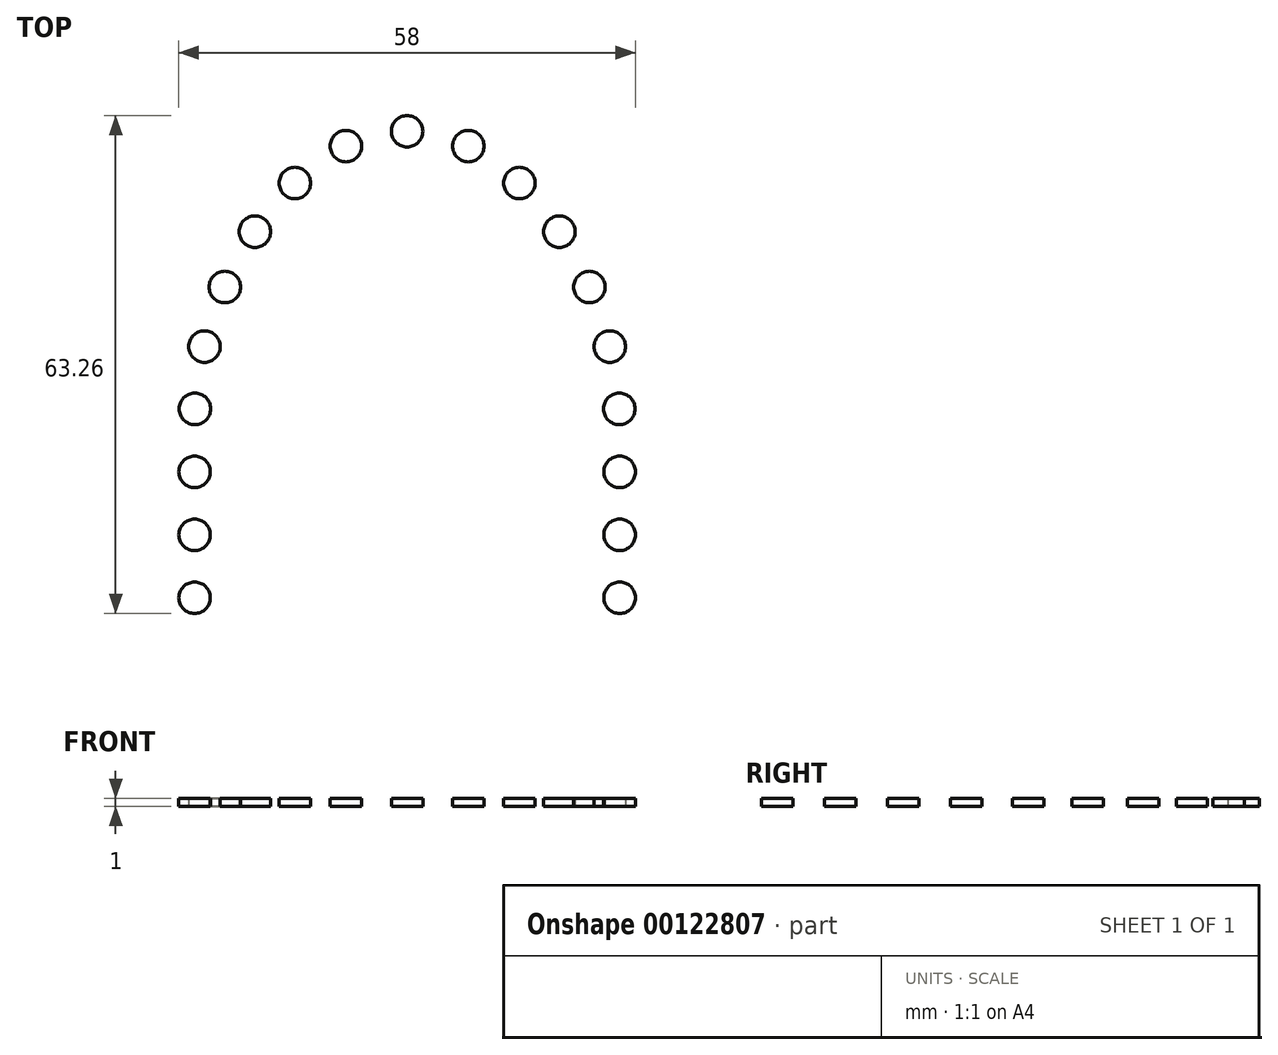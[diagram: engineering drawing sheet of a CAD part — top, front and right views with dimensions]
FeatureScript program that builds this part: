
annotation { "Feature Type Name" : "Feature", "Feature Type Description" : "" }
export const myFeature = defineFeature(function(context is Context, id is Id, definition is map)
    precondition{}
    {
        {
            var Q0;
            Q0=qCreatedBy(makeId("Top.planeOp"),FACE);
            var sketch = newSketch(context, id + "F0", { "sketchPlane" : qUnion([Q0])});
            skLineSegment(sketch, "E0.top", {"start": v(-35, -35) * mm, "end": v(35, -35) * mm});
            skPoint(sketch, "E0.middle", {"position": v(0, 13.14) * mm});
            skPoint(sketch, "E1", {"position": v(0, 0) * mm});
            skCircle(sketch, "E2", {"center": v(0, 0) * mm, "radius": 35 * mm});
            skPoint(sketch, "E3.visualSharp", {"position": v(-35, -35) * mm});
            skPoint(sketch, "E4.visualSharp", {"position": v(35, -35) * mm});
            skPoint(sketch, "E5", {"position": v(-35, 0) * mm});
            skPoint(sketch, "E6", {"position": v(35, 0) * mm});
            skFitSpline(sketch, "E7", {"points": [v(0, 45) * mm, v(-35, 0) * mm], "startDerivative": vector(-60.6, 0) * mm, "endDerivative": vector(0, -60.15) * mm});
            skLineSegment(sketch, "E8", {"start": v(-35, 0) * mm, "end": v(-35, -35) * mm});
            skLineSegment(sketch, "E9", {"start": v(35, 0) * mm, "end": v(35, -35) * mm});
            skFitSpline(sketch, "E10.MirrorCS", {"points": [v(0, 45) * mm, v(35, 0) * mm], "startDerivative": vector(60.6, 0) * mm, "endDerivative": vector(0, -60.15) * mm});
            skFitSpline(sketch, "E11.0", {"points": [v(0, 37) * mm, v(-0.85, 37) * mm, v(-2.51, 36.87) * mm, v(-4.95, 36.3) * mm, v(-7.36, 35.37) * mm, v(-10.54, 33.64) * mm, v(-14.42, 30.55) * mm, v(-18.67, 25.54) * mm, v(-22.24, 19.56) * mm, v(-24.95, 13) * mm, v(-26.62, 6.3) * mm, v(-27, 2.01) * mm, v(-27, 0) * mm]});
            skPoint(sketch, "E12", {"position": v(0, 37) * mm});
            skPoint(sketch, "E13", {"position": v(-7.77, 35.11) * mm});
            skPoint(sketch, "E14", {"position": v(-14.26, 30.43) * mm});
            skPoint(sketch, "E15", {"position": v(-19.34, 24.24) * mm});
            skPoint(sketch, "E16", {"position": v(-23.15, 17.21) * mm});
            skPoint(sketch, "E17", {"position": v(-25.74, 9.64) * mm});
            skLineSegment(sketch, "E18", {"start": v(-27, 0) * mm, "end": v(-27, -35) * mm});
            skPoint(sketch, "E19", {"position": v(-26.96, 1.74) * mm});
            skPoint(sketch, "E20", {"position": v(-27, -6.26) * mm});
            skPoint(sketch, "E21", {"position": v(-27, -14.26) * mm});
            skPoint(sketch, "E22", {"position": v(-27, -22.26) * mm});
            skPoint(sketch, "E23", {"position": v(-27, -30.26) * mm});
            skLineSegment(sketch, "E24.MirrorCS", {"start": v(27, 0) * mm, "end": v(27, -35) * mm});
            skPoint(sketch, "E25.MirrorP", {"position": v(7.77, 35.11) * mm});
            skPoint(sketch, "E26.MirrorP", {"position": v(14.26, 30.43) * mm});
            skPoint(sketch, "E27.MirrorP", {"position": v(19.34, 24.24) * mm});
            skPoint(sketch, "E28.MirrorP", {"position": v(23.15, 17.21) * mm});
            skPoint(sketch, "E29.MirrorP", {"position": v(25.74, 9.64) * mm});
            skPoint(sketch, "E30.MirrorP", {"position": v(26.96, 1.74) * mm});
            skPoint(sketch, "E31.MirrorP", {"position": v(27, -6.26) * mm});
            skPoint(sketch, "E32.MirrorP", {"position": v(27, -14.26) * mm});
            skPoint(sketch, "E33.MirrorP", {"position": v(27, -22.26) * mm});
            skPoint(sketch, "E34.MirrorP", {"position": v(27, -30.26) * mm});
            skFitSpline(sketch, "E35.0", {"points": [v(0, 37) * mm, v(0.85, 37) * mm, v(2.51, 36.87) * mm, v(4.95, 36.3) * mm, v(7.36, 35.37) * mm, v(10.54, 33.64) * mm, v(14.42, 30.55) * mm, v(18.67, 25.54) * mm, v(22.24, 19.56) * mm, v(24.95, 13) * mm, v(26.62, 6.3) * mm, v(27, 2.01) * mm, v(27, 0) * mm]});
            skCircle(sketch, "E36", {"center": v(0, 37) * mm, "radius": 2 * mm});
            skCircle(sketch, "E37", {"center": v(-7.77, 35.11) * mm, "radius": 2 * mm});
            skCircle(sketch, "E38", {"center": v(-14.26, 30.43) * mm, "radius": 2 * mm});
            skCircle(sketch, "E39", {"center": v(-19.34, 24.24) * mm, "radius": 2 * mm});
            skCircle(sketch, "E40", {"center": v(-23.15, 17.21) * mm, "radius": 2 * mm});
            skCircle(sketch, "E41", {"center": v(-25.74, 9.64) * mm, "radius": 2 * mm});
            skCircle(sketch, "E42", {"center": v(-26.96, 1.74) * mm, "radius": 2 * mm});
            skCircle(sketch, "E43", {"center": v(-27, -6.26) * mm, "radius": 2 * mm});
            skCircle(sketch, "E44", {"center": v(-27, -14.26) * mm, "radius": 2 * mm});
            skCircle(sketch, "E45", {"center": v(-27, -22.26) * mm, "radius": 2 * mm});
            skCircle(sketch, "E46", {"center": v(-27, -30.26) * mm, "radius": 2 * mm});
            skCircle(sketch, "E47.MirrorC", {"center": v(7.77, 35.11) * mm, "radius": 2 * mm});
            skCircle(sketch, "E48.MirrorC", {"center": v(14.26, 30.43) * mm, "radius": 2 * mm});
            skCircle(sketch, "E49.MirrorC", {"center": v(19.34, 24.24) * mm, "radius": 2 * mm});
            skCircle(sketch, "E50.MirrorC", {"center": v(23.15, 17.21) * mm, "radius": 2 * mm});
            skCircle(sketch, "E51.MirrorC", {"center": v(25.74, 9.64) * mm, "radius": 2 * mm});
            skCircle(sketch, "E52.MirrorC", {"center": v(26.96, 1.74) * mm, "radius": 2 * mm});
            skCircle(sketch, "E53.MirrorC", {"center": v(27, -6.26) * mm, "radius": 2 * mm});
            skCircle(sketch, "E54.MirrorC", {"center": v(27, -14.26) * mm, "radius": 2 * mm});
            skCircle(sketch, "E55.MirrorC", {"center": v(27, -22.26) * mm, "radius": 2 * mm});
            skCircle(sketch, "E56.MirrorC", {"center": v(27, -30.26) * mm, "radius": 2 * mm});
            skSolve(sketch);
        }
        {
            var Q0;
            {var subQ0=sQuery(id+"F0.wireOp",EDGE,"E45");var subQ1=sQuery(id+"F0.wireOp",EDGE,"E2");var subQ2=makeQuery(id+"F0.imprint","INTERSECT",VERTEX,{"disambiguationData":[OD(0.0)],"derivedFrom":[subQ1,subQ0]});Q0=makeQuery(id+"F0.imprint","IMPRINT",FACE,{"disambiguationData":[TD([[makeQuery(id+"F0.imprint","IMPRINT",EDGE,{"disambiguationData":[TD([[subQ2,-1.0]])],"derivedFrom":subQ1}),-1.0]])]});}
            var Q1;
            {var subQ0=sQuery(id+"F0.wireOp",EDGE,"E18");var subQ1=sQuery(id+"F0.wireOp",EDGE,"E2");var subQ2=makeQuery(id+"F0.imprint","INTERSECT",VERTEX,{"derivedFrom":[subQ1,subQ0]});Q1=makeQuery(id+"F0.imprint","IMPRINT",FACE,{"disambiguationData":[TD([[makeQuery(id+"F0.imprint","IMPRINT",EDGE,{"disambiguationData":[TD([[subQ2,-1.0]])],"derivedFrom":subQ1}),-1.0]])]});}
            var Q2;
            {var subQ0=sQuery(id+"F0.wireOp",EDGE,"E18");var subQ1=sQuery(id+"F0.wireOp",EDGE,"E2");var subQ2=makeQuery(id+"F0.imprint","INTERSECT",VERTEX,{"derivedFrom":[subQ1,subQ0]});Q2=makeQuery(id+"F0.imprint","IMPRINT",FACE,{"disambiguationData":[TD([[makeQuery(id+"F0.imprint","IMPRINT",EDGE,{"disambiguationData":[TD([[subQ2,-1.0]])],"derivedFrom":subQ1}),1.0]])]});}
            var Q3;
            {var subQ0=sQuery(id+"F0.wireOp",EDGE,"E45");var subQ1=sQuery(id+"F0.wireOp",EDGE,"E2");var subQ2=makeQuery(id+"F0.imprint","INTERSECT",VERTEX,{"disambiguationData":[OD(0.0)],"derivedFrom":[subQ1,subQ0]});Q3=makeQuery(id+"F0.imprint","IMPRINT",FACE,{"disambiguationData":[TD([[makeQuery(id+"F0.imprint","IMPRINT",EDGE,{"disambiguationData":[TD([[subQ2,-1.0]])],"derivedFrom":subQ1}),1.0]])]});}
            var Q4;
            {var subQ0=sQuery(id+"F0.wireOp",EDGE,"E44");var subQ1=sQuery(id+"F0.wireOp",EDGE,"E18");var subQ2=makeQuery(id+"F0.imprint","INTERSECT",VERTEX,{"disambiguationData":[OD(0.0)],"derivedFrom":[subQ1,subQ0]});Q4=makeQuery(id+"F0.imprint","IMPRINT",FACE,{"disambiguationData":[TD([[makeQuery(id+"F0.imprint","IMPRINT",EDGE,{"disambiguationData":[TD([[subQ2,-1.0]])],"derivedFrom":subQ1}),-1.0]])]});}
            var Q5;
            {var subQ0=sQuery(id+"F0.wireOp",EDGE,"E44");var subQ1=sQuery(id+"F0.wireOp",EDGE,"E18");var subQ2=makeQuery(id+"F0.imprint","INTERSECT",VERTEX,{"disambiguationData":[OD(0.0)],"derivedFrom":[subQ1,subQ0]});Q5=makeQuery(id+"F0.imprint","IMPRINT",FACE,{"disambiguationData":[TD([[makeQuery(id+"F0.imprint","IMPRINT",EDGE,{"disambiguationData":[TD([[subQ2,-1.0]])],"derivedFrom":subQ1}),1.0]])]});}
            var Q6;
            {var subQ0=sQuery(id+"F0.wireOp",EDGE,"E43");var subQ1=sQuery(id+"F0.wireOp",EDGE,"E18");var subQ2=makeQuery(id+"F0.imprint","INTERSECT",VERTEX,{"disambiguationData":[OD(0.0)],"derivedFrom":[subQ1,subQ0]});Q6=makeQuery(id+"F0.imprint","IMPRINT",FACE,{"disambiguationData":[TD([[makeQuery(id+"F0.imprint","IMPRINT",EDGE,{"disambiguationData":[TD([[subQ2,-1.0]])],"derivedFrom":subQ1}),1.0]])]});}
            var Q7;
            {var subQ0=sQuery(id+"F0.wireOp",EDGE,"E43");var subQ1=sQuery(id+"F0.wireOp",EDGE,"E18");var subQ2=makeQuery(id+"F0.imprint","INTERSECT",VERTEX,{"disambiguationData":[OD(0.0)],"derivedFrom":[subQ1,subQ0]});Q7=makeQuery(id+"F0.imprint","IMPRINT",FACE,{"disambiguationData":[TD([[makeQuery(id+"F0.imprint","IMPRINT",EDGE,{"disambiguationData":[TD([[subQ2,-1.0]])],"derivedFrom":subQ1}),-1.0]])]});}
            var Q8;
            {var subQ0=sQuery(id+"F0.wireOp",EDGE,"E18");var subQ1=sQuery(id+"F0.wireOp",EDGE,"E11.0");var subQ2=makeQuery(id+"F0.imprint","INTERSECT",VERTEX,{"derivedFrom":[subQ1,subQ0]});Q8=makeQuery(id+"F0.imprint","IMPRINT",FACE,{"disambiguationData":[TD([[makeQuery(id+"F0.imprint","IMPRINT",EDGE,{"disambiguationData":[TD([[subQ2,1.0]])],"derivedFrom":subQ1}),-1.0]])]});}
            var Q9;
            {var subQ0=sQuery(id+"F0.wireOp",EDGE,"E18");var subQ1=sQuery(id+"F0.wireOp",EDGE,"E11.0");var subQ2=makeQuery(id+"F0.imprint","INTERSECT",VERTEX,{"derivedFrom":[subQ1,subQ0]});Q9=makeQuery(id+"F0.imprint","IMPRINT",FACE,{"disambiguationData":[TD([[makeQuery(id+"F0.imprint","IMPRINT",EDGE,{"disambiguationData":[TD([[subQ2,1.0]])],"derivedFrom":subQ1}),1.0]])]});}
            var Q10;
            {var subQ0=sQuery(id+"F0.wireOp",EDGE,"E41");var subQ1=sQuery(id+"F0.wireOp",EDGE,"E11.0");var subQ2=makeQuery(id+"F0.imprint","INTERSECT",VERTEX,{"disambiguationData":[OD(0.0)],"derivedFrom":[subQ1,subQ0]});Q10=makeQuery(id+"F0.imprint","IMPRINT",FACE,{"disambiguationData":[TD([[makeQuery(id+"F0.imprint","IMPRINT",EDGE,{"disambiguationData":[TD([[subQ2,-1.0]])],"derivedFrom":subQ1}),1.0]])]});}
            var Q11;
            {var subQ0=sQuery(id+"F0.wireOp",EDGE,"E41");var subQ1=sQuery(id+"F0.wireOp",EDGE,"E11.0");var subQ2=makeQuery(id+"F0.imprint","INTERSECT",VERTEX,{"disambiguationData":[OD(0.0)],"derivedFrom":[subQ1,subQ0]});Q11=makeQuery(id+"F0.imprint","IMPRINT",FACE,{"disambiguationData":[TD([[makeQuery(id+"F0.imprint","IMPRINT",EDGE,{"disambiguationData":[TD([[subQ2,-1.0]])],"derivedFrom":subQ1}),-1.0]])]});}
            var Q12;
            {var subQ0=sQuery(id+"F0.wireOp",EDGE,"E40");var subQ1=sQuery(id+"F0.wireOp",EDGE,"E11.0");var subQ2=makeQuery(id+"F0.imprint","INTERSECT",VERTEX,{"disambiguationData":[OD(0.0)],"derivedFrom":[subQ1,subQ0]});Q12=makeQuery(id+"F0.imprint","IMPRINT",FACE,{"disambiguationData":[TD([[makeQuery(id+"F0.imprint","IMPRINT",EDGE,{"disambiguationData":[TD([[subQ2,-1.0]])],"derivedFrom":subQ1}),1.0]])]});}
            var Q13;
            {var subQ0=sQuery(id+"F0.wireOp",EDGE,"E40");var subQ1=sQuery(id+"F0.wireOp",EDGE,"E11.0");var subQ2=makeQuery(id+"F0.imprint","INTERSECT",VERTEX,{"disambiguationData":[OD(0.0)],"derivedFrom":[subQ1,subQ0]});Q13=makeQuery(id+"F0.imprint","IMPRINT",FACE,{"disambiguationData":[TD([[makeQuery(id+"F0.imprint","IMPRINT",EDGE,{"disambiguationData":[TD([[subQ2,-1.0]])],"derivedFrom":subQ1}),-1.0]])]});}
            var Q14;
            {var subQ0=sQuery(id+"F0.wireOp",EDGE,"E39");var subQ1=sQuery(id+"F0.wireOp",EDGE,"E11.0");var subQ2=makeQuery(id+"F0.imprint","INTERSECT",VERTEX,{"disambiguationData":[OD(0.0)],"derivedFrom":[subQ1,subQ0]});Q14=makeQuery(id+"F0.imprint","IMPRINT",FACE,{"disambiguationData":[TD([[makeQuery(id+"F0.imprint","IMPRINT",EDGE,{"disambiguationData":[TD([[subQ2,-1.0]])],"derivedFrom":subQ1}),1.0]])]});}
            var Q15;
            {var subQ0=sQuery(id+"F0.wireOp",EDGE,"E39");var subQ1=sQuery(id+"F0.wireOp",EDGE,"E11.0");var subQ2=makeQuery(id+"F0.imprint","INTERSECT",VERTEX,{"disambiguationData":[OD(0.0)],"derivedFrom":[subQ1,subQ0]});Q15=makeQuery(id+"F0.imprint","IMPRINT",FACE,{"disambiguationData":[TD([[makeQuery(id+"F0.imprint","IMPRINT",EDGE,{"disambiguationData":[TD([[subQ2,-1.0]])],"derivedFrom":subQ1}),-1.0]])]});}
            var Q16;
            {var subQ0=sQuery(id+"F0.wireOp",EDGE,"E38");var subQ1=sQuery(id+"F0.wireOp",EDGE,"E11.0");var subQ2=makeQuery(id+"F0.imprint","INTERSECT",VERTEX,{"disambiguationData":[OD(0.0)],"derivedFrom":[subQ1,subQ0]});Q16=makeQuery(id+"F0.imprint","IMPRINT",FACE,{"disambiguationData":[TD([[makeQuery(id+"F0.imprint","IMPRINT",EDGE,{"disambiguationData":[TD([[subQ2,-1.0]])],"derivedFrom":subQ1}),1.0]])]});}
            var Q17;
            {var subQ0=sQuery(id+"F0.wireOp",EDGE,"E38");var subQ1=sQuery(id+"F0.wireOp",EDGE,"E2");var subQ2=makeQuery(id+"F0.imprint","INTERSECT",VERTEX,{"disambiguationData":[OD(0.0)],"derivedFrom":[subQ1,subQ0]});Q17=makeQuery(id+"F0.imprint","IMPRINT",FACE,{"disambiguationData":[TD([[makeQuery(id+"F0.imprint","IMPRINT",EDGE,{"disambiguationData":[TD([[subQ2,-1.0]])],"derivedFrom":subQ1}),1.0]])]});}
            var Q18;
            {var subQ0=sQuery(id+"F0.wireOp",EDGE,"E38");var subQ1=sQuery(id+"F0.wireOp",EDGE,"E2");var subQ2=makeQuery(id+"F0.imprint","INTERSECT",VERTEX,{"disambiguationData":[OD(0.0)],"derivedFrom":[subQ1,subQ0]});Q18=makeQuery(id+"F0.imprint","IMPRINT",FACE,{"disambiguationData":[TD([[makeQuery(id+"F0.imprint","IMPRINT",EDGE,{"disambiguationData":[TD([[subQ2,-1.0]])],"derivedFrom":subQ1}),-1.0]])]});}
            var Q19;
            {var subQ0=sQuery(id+"F0.wireOp",EDGE,"E37");var subQ1=sQuery(id+"F0.wireOp",EDGE,"E2");var subQ2=makeQuery(id+"F0.imprint","INTERSECT",VERTEX,{"disambiguationData":[OD(0.0)],"derivedFrom":[subQ1,subQ0]});Q19=makeQuery(id+"F0.imprint","IMPRINT",FACE,{"disambiguationData":[TD([[makeQuery(id+"F0.imprint","IMPRINT",EDGE,{"disambiguationData":[TD([[subQ2,-1.0]])],"derivedFrom":subQ1}),1.0]])]});}
            var Q20;
            {var subQ0=sQuery(id+"F0.wireOp",EDGE,"E37");var subQ1=sQuery(id+"F0.wireOp",EDGE,"E2");var subQ2=makeQuery(id+"F0.imprint","INTERSECT",VERTEX,{"disambiguationData":[OD(0.0)],"derivedFrom":[subQ1,subQ0]});Q20=makeQuery(id+"F0.imprint","IMPRINT",FACE,{"disambiguationData":[TD([[makeQuery(id+"F0.imprint","IMPRINT",EDGE,{"disambiguationData":[TD([[subQ2,-1.0]])],"derivedFrom":subQ1}),-1.0]])]});}
            var Q21;
            {var subQ0=sQuery(id+"F0.wireOp",EDGE,"E37");var subQ1=sQuery(id+"F0.wireOp",EDGE,"E11.0");var subQ2=makeQuery(id+"F0.imprint","INTERSECT",VERTEX,{"disambiguationData":[OD(0.0)],"derivedFrom":[subQ1,subQ0]});Q21=makeQuery(id+"F0.imprint","IMPRINT",FACE,{"disambiguationData":[TD([[makeQuery(id+"F0.imprint","IMPRINT",EDGE,{"disambiguationData":[TD([[subQ2,-1.0]])],"derivedFrom":subQ1}),-1.0]])]});}
            var Q22;
            {var subQ0=sQuery(id+"F0.wireOp",EDGE,"E35.0");var subQ1=sQuery(id+"F0.wireOp",EDGE,"E11.0");var subQ2=makeQuery(id+"F0.imprint","INTERSECT",VERTEX,{"derivedFrom":[subQ1,subQ0]});Q22=makeQuery(id+"F0.imprint","IMPRINT",FACE,{"disambiguationData":[TD([[makeQuery(id+"F0.imprint","IMPRINT",EDGE,{"disambiguationData":[TD([[subQ2,-1.0]])],"derivedFrom":subQ1}),-1.0]])]});}
            var Q23;
            {var subQ0=sQuery(id+"F0.wireOp",EDGE,"E47.MirrorC");var subQ1=sQuery(id+"F0.wireOp",EDGE,"E35.0");var subQ2=makeQuery(id+"F0.imprint","INTERSECT",VERTEX,{"disambiguationData":[OD(0.0)],"derivedFrom":[subQ1,subQ0]});Q23=makeQuery(id+"F0.imprint","IMPRINT",FACE,{"disambiguationData":[TD([[makeQuery(id+"F0.imprint","IMPRINT",EDGE,{"disambiguationData":[TD([[subQ2,-1.0]])],"derivedFrom":subQ1}),1.0]])]});}
            var Q24;
            {var subQ0=sQuery(id+"F0.wireOp",EDGE,"E47.MirrorC");var subQ1=sQuery(id+"F0.wireOp",EDGE,"E2");var subQ2=makeQuery(id+"F0.imprint","INTERSECT",VERTEX,{"disambiguationData":[OD(0.0)],"derivedFrom":[subQ1,subQ0]});Q24=makeQuery(id+"F0.imprint","IMPRINT",FACE,{"disambiguationData":[TD([[makeQuery(id+"F0.imprint","IMPRINT",EDGE,{"disambiguationData":[TD([[subQ2,-1.0]])],"derivedFrom":subQ1}),-1.0]])]});}
            var Q25;
            {var subQ0=sQuery(id+"F0.wireOp",EDGE,"E47.MirrorC");var subQ1=sQuery(id+"F0.wireOp",EDGE,"E2");var subQ2=makeQuery(id+"F0.imprint","INTERSECT",VERTEX,{"disambiguationData":[OD(0.0)],"derivedFrom":[subQ1,subQ0]});Q25=makeQuery(id+"F0.imprint","IMPRINT",FACE,{"disambiguationData":[TD([[makeQuery(id+"F0.imprint","IMPRINT",EDGE,{"disambiguationData":[TD([[subQ2,-1.0]])],"derivedFrom":subQ1}),1.0]])]});}
            var Q26;
            {var subQ0=sQuery(id+"F0.wireOp",EDGE,"E48.MirrorC");var subQ1=sQuery(id+"F0.wireOp",EDGE,"E2");var subQ2=makeQuery(id+"F0.imprint","INTERSECT",VERTEX,{"disambiguationData":[OD(0.0)],"derivedFrom":[subQ1,subQ0]});Q26=makeQuery(id+"F0.imprint","IMPRINT",FACE,{"disambiguationData":[TD([[makeQuery(id+"F0.imprint","IMPRINT",EDGE,{"disambiguationData":[TD([[subQ2,-1.0]])],"derivedFrom":subQ1}),1.0]])]});}
            var Q27;
            {var subQ0=sQuery(id+"F0.wireOp",EDGE,"E48.MirrorC");var subQ1=sQuery(id+"F0.wireOp",EDGE,"E35.0");var subQ2=makeQuery(id+"F0.imprint","INTERSECT",VERTEX,{"disambiguationData":[OD(0.0)],"derivedFrom":[subQ1,subQ0]});Q27=makeQuery(id+"F0.imprint","IMPRINT",FACE,{"disambiguationData":[TD([[makeQuery(id+"F0.imprint","IMPRINT",EDGE,{"disambiguationData":[TD([[subQ2,-1.0]])],"derivedFrom":subQ1}),-1.0]])]});}
            var Q28;
            {var subQ0=sQuery(id+"F0.wireOp",EDGE,"E48.MirrorC");var subQ1=sQuery(id+"F0.wireOp",EDGE,"E2");var subQ2=makeQuery(id+"F0.imprint","INTERSECT",VERTEX,{"disambiguationData":[OD(0.0)],"derivedFrom":[subQ1,subQ0]});Q28=makeQuery(id+"F0.imprint","IMPRINT",FACE,{"disambiguationData":[TD([[makeQuery(id+"F0.imprint","IMPRINT",EDGE,{"disambiguationData":[TD([[subQ2,-1.0]])],"derivedFrom":subQ1}),-1.0]])]});}
            var Q29;
            {var subQ0=sQuery(id+"F0.wireOp",EDGE,"E49.MirrorC");var subQ1=sQuery(id+"F0.wireOp",EDGE,"E35.0");var subQ2=makeQuery(id+"F0.imprint","INTERSECT",VERTEX,{"disambiguationData":[OD(0.0)],"derivedFrom":[subQ1,subQ0]});Q29=makeQuery(id+"F0.imprint","IMPRINT",FACE,{"disambiguationData":[TD([[makeQuery(id+"F0.imprint","IMPRINT",EDGE,{"disambiguationData":[TD([[subQ2,-1.0]])],"derivedFrom":subQ1}),1.0]])]});}
            var Q30;
            {var subQ0=sQuery(id+"F0.wireOp",EDGE,"E49.MirrorC");var subQ1=sQuery(id+"F0.wireOp",EDGE,"E35.0");var subQ2=makeQuery(id+"F0.imprint","INTERSECT",VERTEX,{"disambiguationData":[OD(0.0)],"derivedFrom":[subQ1,subQ0]});Q30=makeQuery(id+"F0.imprint","IMPRINT",FACE,{"disambiguationData":[TD([[makeQuery(id+"F0.imprint","IMPRINT",EDGE,{"disambiguationData":[TD([[subQ2,-1.0]])],"derivedFrom":subQ1}),-1.0]])]});}
            var Q31;
            {var subQ0=sQuery(id+"F0.wireOp",EDGE,"E50.MirrorC");var subQ1=sQuery(id+"F0.wireOp",EDGE,"E35.0");var subQ2=makeQuery(id+"F0.imprint","INTERSECT",VERTEX,{"disambiguationData":[OD(0.0)],"derivedFrom":[subQ1,subQ0]});Q31=makeQuery(id+"F0.imprint","IMPRINT",FACE,{"disambiguationData":[TD([[makeQuery(id+"F0.imprint","IMPRINT",EDGE,{"disambiguationData":[TD([[subQ2,-1.0]])],"derivedFrom":subQ1}),1.0]])]});}
            var Q32;
            {var subQ0=sQuery(id+"F0.wireOp",EDGE,"E50.MirrorC");var subQ1=sQuery(id+"F0.wireOp",EDGE,"E35.0");var subQ2=makeQuery(id+"F0.imprint","INTERSECT",VERTEX,{"disambiguationData":[OD(0.0)],"derivedFrom":[subQ1,subQ0]});Q32=makeQuery(id+"F0.imprint","IMPRINT",FACE,{"disambiguationData":[TD([[makeQuery(id+"F0.imprint","IMPRINT",EDGE,{"disambiguationData":[TD([[subQ2,-1.0]])],"derivedFrom":subQ1}),-1.0]])]});}
            var Q33;
            {var subQ0=sQuery(id+"F0.wireOp",EDGE,"E51.MirrorC");var subQ1=sQuery(id+"F0.wireOp",EDGE,"E35.0");var subQ2=makeQuery(id+"F0.imprint","INTERSECT",VERTEX,{"disambiguationData":[OD(0.0)],"derivedFrom":[subQ1,subQ0]});Q33=makeQuery(id+"F0.imprint","IMPRINT",FACE,{"disambiguationData":[TD([[makeQuery(id+"F0.imprint","IMPRINT",EDGE,{"disambiguationData":[TD([[subQ2,-1.0]])],"derivedFrom":subQ1}),1.0]])]});}
            var Q34;
            {var subQ0=sQuery(id+"F0.wireOp",EDGE,"E51.MirrorC");var subQ1=sQuery(id+"F0.wireOp",EDGE,"E35.0");var subQ2=makeQuery(id+"F0.imprint","INTERSECT",VERTEX,{"disambiguationData":[OD(0.0)],"derivedFrom":[subQ1,subQ0]});Q34=makeQuery(id+"F0.imprint","IMPRINT",FACE,{"disambiguationData":[TD([[makeQuery(id+"F0.imprint","IMPRINT",EDGE,{"disambiguationData":[TD([[subQ2,-1.0]])],"derivedFrom":subQ1}),-1.0]])]});}
            var Q35;
            {var subQ0=sQuery(id+"F0.wireOp",EDGE,"E35.0");var subQ1=sQuery(id+"F0.wireOp",EDGE,"E24.MirrorCS");var subQ2=makeQuery(id+"F0.imprint","INTERSECT",VERTEX,{"derivedFrom":[subQ1,subQ0]});Q35=makeQuery(id+"F0.imprint","IMPRINT",FACE,{"disambiguationData":[TD([[makeQuery(id+"F0.imprint","IMPRINT",EDGE,{"disambiguationData":[TD([[subQ2,-1.0]])],"derivedFrom":subQ1}),1.0]])]});}
            var Q36;
            {var subQ0=sQuery(id+"F0.wireOp",EDGE,"E35.0");var subQ1=sQuery(id+"F0.wireOp",EDGE,"E24.MirrorCS");var subQ2=makeQuery(id+"F0.imprint","INTERSECT",VERTEX,{"derivedFrom":[subQ1,subQ0]});Q36=makeQuery(id+"F0.imprint","IMPRINT",FACE,{"disambiguationData":[TD([[makeQuery(id+"F0.imprint","IMPRINT",EDGE,{"disambiguationData":[TD([[subQ2,-1.0]])],"derivedFrom":subQ1}),-1.0]])]});}
            var Q37;
            {var subQ0=sQuery(id+"F0.wireOp",EDGE,"E53.MirrorC");var subQ1=sQuery(id+"F0.wireOp",EDGE,"E24.MirrorCS");var subQ2=makeQuery(id+"F0.imprint","INTERSECT",VERTEX,{"disambiguationData":[OD(0.0)],"derivedFrom":[subQ1,subQ0]});Q37=makeQuery(id+"F0.imprint","IMPRINT",FACE,{"disambiguationData":[TD([[makeQuery(id+"F0.imprint","IMPRINT",EDGE,{"disambiguationData":[TD([[subQ2,-1.0]])],"derivedFrom":subQ1}),1.0]])]});}
            var Q38;
            {var subQ0=sQuery(id+"F0.wireOp",EDGE,"E53.MirrorC");var subQ1=sQuery(id+"F0.wireOp",EDGE,"E24.MirrorCS");var subQ2=makeQuery(id+"F0.imprint","INTERSECT",VERTEX,{"disambiguationData":[OD(0.0)],"derivedFrom":[subQ1,subQ0]});Q38=makeQuery(id+"F0.imprint","IMPRINT",FACE,{"disambiguationData":[TD([[makeQuery(id+"F0.imprint","IMPRINT",EDGE,{"disambiguationData":[TD([[subQ2,-1.0]])],"derivedFrom":subQ1}),-1.0]])]});}
            var Q39;
            {var subQ0=sQuery(id+"F0.wireOp",EDGE,"E54.MirrorC");var subQ1=sQuery(id+"F0.wireOp",EDGE,"E24.MirrorCS");var subQ2=makeQuery(id+"F0.imprint","INTERSECT",VERTEX,{"disambiguationData":[OD(0.0)],"derivedFrom":[subQ1,subQ0]});Q39=makeQuery(id+"F0.imprint","IMPRINT",FACE,{"disambiguationData":[TD([[makeQuery(id+"F0.imprint","IMPRINT",EDGE,{"disambiguationData":[TD([[subQ2,-1.0]])],"derivedFrom":subQ1}),-1.0]])]});}
            var Q40;
            {var subQ0=sQuery(id+"F0.wireOp",EDGE,"E54.MirrorC");var subQ1=sQuery(id+"F0.wireOp",EDGE,"E24.MirrorCS");var subQ2=makeQuery(id+"F0.imprint","INTERSECT",VERTEX,{"disambiguationData":[OD(0.0)],"derivedFrom":[subQ1,subQ0]});Q40=makeQuery(id+"F0.imprint","IMPRINT",FACE,{"disambiguationData":[TD([[makeQuery(id+"F0.imprint","IMPRINT",EDGE,{"disambiguationData":[TD([[subQ2,-1.0]])],"derivedFrom":subQ1}),1.0]])]});}
            var Q41;
            {var subQ0=sQuery(id+"F0.wireOp",EDGE,"E55.MirrorC");var subQ1=sQuery(id+"F0.wireOp",EDGE,"E2");var subQ2=makeQuery(id+"F0.imprint","INTERSECT",VERTEX,{"disambiguationData":[OD(0.0)],"derivedFrom":[subQ1,subQ0]});Q41=makeQuery(id+"F0.imprint","IMPRINT",FACE,{"disambiguationData":[TD([[makeQuery(id+"F0.imprint","IMPRINT",EDGE,{"disambiguationData":[TD([[subQ2,-1.0]])],"derivedFrom":subQ1}),1.0]])]});}
            var Q42;
            {var subQ0=sQuery(id+"F0.wireOp",EDGE,"E24.MirrorCS");var subQ1=sQuery(id+"F0.wireOp",EDGE,"E2");var subQ2=makeQuery(id+"F0.imprint","INTERSECT",VERTEX,{"derivedFrom":[subQ1,subQ0]});Q42=makeQuery(id+"F0.imprint","IMPRINT",FACE,{"disambiguationData":[TD([[makeQuery(id+"F0.imprint","IMPRINT",EDGE,{"disambiguationData":[TD([[subQ2,-1.0]])],"derivedFrom":subQ1}),-1.0]])]});}
            var Q43;
            {var subQ0=sQuery(id+"F0.wireOp",EDGE,"E24.MirrorCS");var subQ1=sQuery(id+"F0.wireOp",EDGE,"E2");var subQ2=makeQuery(id+"F0.imprint","INTERSECT",VERTEX,{"derivedFrom":[subQ1,subQ0]});Q43=makeQuery(id+"F0.imprint","IMPRINT",FACE,{"disambiguationData":[TD([[makeQuery(id+"F0.imprint","IMPRINT",EDGE,{"disambiguationData":[TD([[subQ2,-1.0]])],"derivedFrom":subQ1}),1.0]])]});}
            var Q44;
            {var subQ0=sQuery(id+"F0.wireOp",EDGE,"E55.MirrorC");var subQ1=sQuery(id+"F0.wireOp",EDGE,"E2");var subQ2=makeQuery(id+"F0.imprint","INTERSECT",VERTEX,{"disambiguationData":[OD(0.0)],"derivedFrom":[subQ1,subQ0]});Q44=makeQuery(id+"F0.imprint","IMPRINT",FACE,{"disambiguationData":[TD([[makeQuery(id+"F0.imprint","IMPRINT",EDGE,{"disambiguationData":[TD([[subQ2,-1.0]])],"derivedFrom":subQ1}),-1.0]])]});}
            var Q45;
            {var subQ0=sQuery(id+"F0.wireOp",EDGE,"E35.0");var subQ1=sQuery(id+"F0.wireOp",EDGE,"E11.0");var subQ2=makeQuery(id+"F0.imprint","INTERSECT",VERTEX,{"derivedFrom":[subQ1,subQ0]});Q45=makeQuery(id+"F0.imprint","IMPRINT",FACE,{"disambiguationData":[TD([[makeQuery(id+"F0.imprint","IMPRINT",EDGE,{"disambiguationData":[TD([[subQ2,-1.0]])],"derivedFrom":subQ1}),1.0]])]});}
            extrude(context, id + "F1", {"entities" : qUnion([Q0, Q1, Q2, Q3, Q4, Q5, Q6, Q7, Q8, Q9, Q10, Q11, Q12, Q13, Q14, Q15, Q16, Q17, Q18, Q19, Q20, Q21, Q22, Q23, Q24, Q25, Q26, Q27, Q28, Q29, Q30, Q31, Q32, Q33, Q34, Q35, Q36, Q37, Q38, Q39, Q40, Q41, Q42, Q43, Q44, Q45]), "depth" : 1 * mm});
        }
    });
